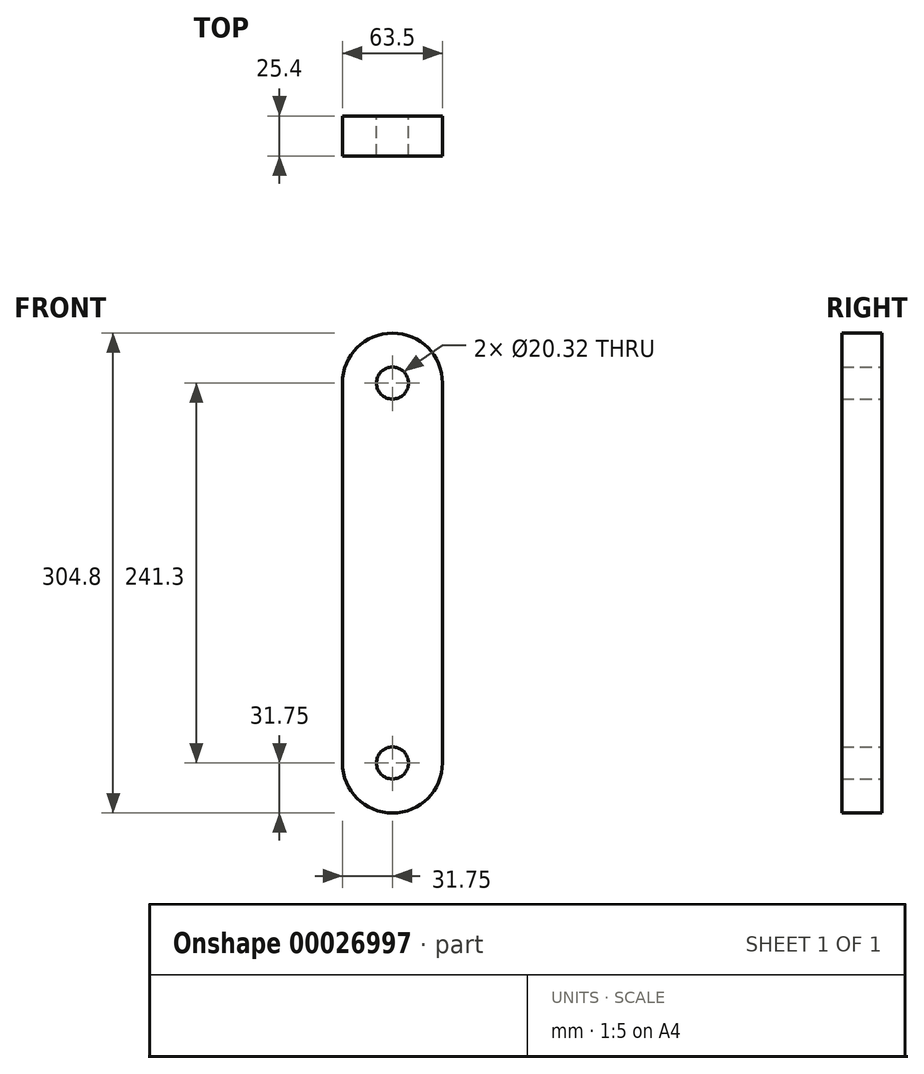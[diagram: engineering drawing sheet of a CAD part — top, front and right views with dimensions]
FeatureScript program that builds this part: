
annotation { "Feature Type Name" : "Feature", "Feature Type Description" : "" }
export const myFeature = defineFeature(function(context is Context, id is Id, definition is map)
    precondition{}
    {
        {
            var Q0;
            Q0=qCreatedBy(makeId("Front.planeOp"),FACE);
            var sketch = newSketch(context, id + "F0", { "sketchPlane" : qUnion([Q0])});
            skCircle(sketch, "E0", {"center": v(31.75, -31.75) * mm, "radius": 31.75 * mm});
            skCircle(sketch, "E1", {"center": v(31.75, -273.05) * mm, "radius": 31.75 * mm});
            skLineSegment(sketch, "E2", {"start": v(0, -31.75) * mm, "end": v(0, -273.05) * mm});
            skLineSegment(sketch, "E3", {"start": v(63.5, -31.75) * mm, "end": v(63.5, -273.05) * mm});
            skCircle(sketch, "E4", {"center": v(31.75, -273.05) * mm, "radius": 10.16 * mm});
            skCircle(sketch, "E5", {"center": v(31.75, -31.75) * mm, "radius": 10.16 * mm});
            skSolve(sketch);
        }
        {
            var Q0;
            Q0=makeQuery(id+"F0.imprint","IMPRINT",FACE,{"disambiguationData":[TD([[makeQuery(id+"F0.imprint","IMPRINT",EDGE,{"derivedFrom":sQuery(id+"F0.wireOp",EDGE,"E5")}),-1.0]])]});
            var Q1;
            {var subQ1=sQuery(id+"F0.wireOp",EDGE,"E2");Q1=makeQuery(id+"F0.imprint","IMPRINT",FACE,{"disambiguationData":[TD([[makeQuery(id+"F0.imprint","IMPRINT",EDGE,{"derivedFrom":subQ1}),1.0]])]});}
            var Q2;
            Q2=makeQuery(id+"F0.imprint","IMPRINT",FACE,{"disambiguationData":[TD([[makeQuery(id+"F0.imprint","IMPRINT",EDGE,{"derivedFrom":sQuery(id+"F0.wireOp",EDGE,"E4")}),-1.0]])]});
            extrude(context, id + "F1", {"entities" : qUnion([Q0, Q1, Q2]), "endBound" : BoundingType.SYMMETRIC, "depth" : 25.4 * mm});
        }
    });
